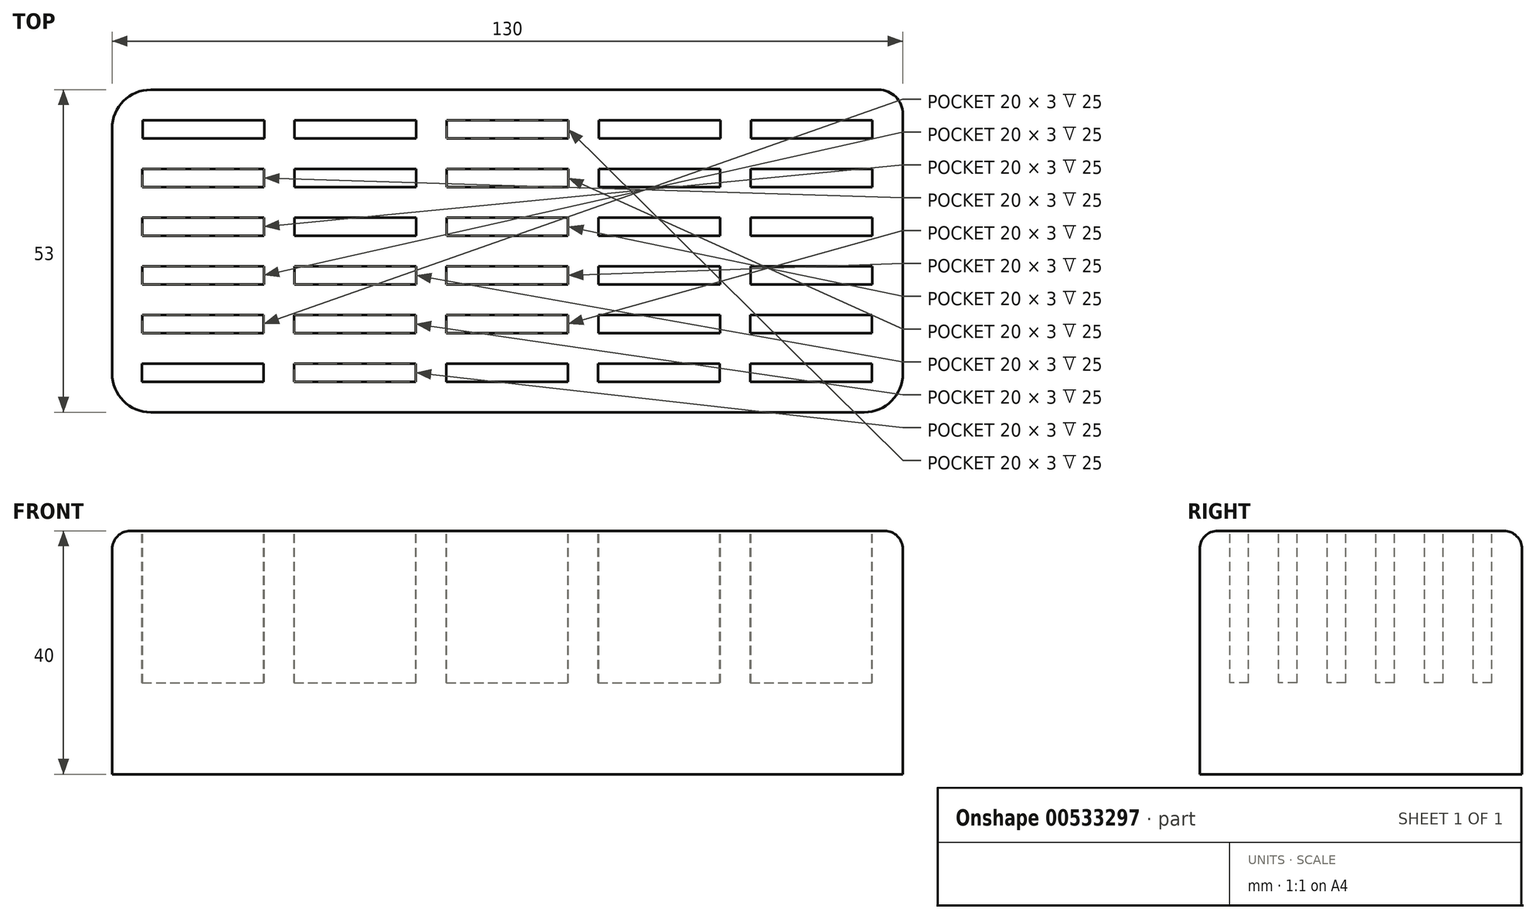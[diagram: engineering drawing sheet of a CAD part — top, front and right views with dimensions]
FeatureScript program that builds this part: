
annotation { "Feature Type Name" : "Feature", "Feature Type Description" : "" }
export const myFeature = defineFeature(function(context is Context, id is Id, definition is map)
    precondition{}
    {
        {
            var Q0;
            Q0=qCreatedBy(makeId("Top.planeOp"),FACE);
            var sketch = newSketch(context, id + "F0", { "sketchPlane" : qUnion([Q0])});
            skLineSegment(sketch, "E0.bottom", {"start": v(-58.22, 28.45) * mm, "end": v(61.43, 28.45) * mm});
            skLineSegment(sketch, "E0.top", {"start": v(-58.22, -24.55) * mm, "end": v(59.08, -24.55) * mm});
            skLineSegment(sketch, "E0.left", {"start": v(-64.57, 22.1) * mm, "end": v(-64.57, -18.2) * mm});
            skLineSegment(sketch, "E0.right", {"start": v(65.43, 24.45) * mm, "end": v(65.43, -18.2) * mm});
            skPoint(sketch, "E1.visualSharp", {"position": v(-64.57, 28.45) * mm});
            skArc(sketch, "E1.filletArc", {"start": v(-58.22, 28.45) * mm, "mid": v(-62.71, 26.59) * mm, "end": v(-64.57, 22.1) * mm});
            skPoint(sketch, "E2.visualSharp", {"position": v(65.43, 28.45) * mm});
            skArc(sketch, "E2.filletArc", {"start": v(65.43, 24.45) * mm, "mid": v(64.26, 27.27) * mm, "end": v(61.43, 28.45) * mm});
            skPoint(sketch, "E3.visualSharp", {"position": v(65.43, -24.55) * mm});
            skArc(sketch, "E3.filletArc", {"start": v(59.08, -24.55) * mm, "mid": v(63.57, -22.7) * mm, "end": v(65.43, -18.2) * mm});
            skPoint(sketch, "E4.visualSharp", {"position": v(-64.57, -24.55) * mm});
            skArc(sketch, "E4.filletArc", {"start": v(-64.57, -18.2) * mm, "mid": v(-62.71, -22.7) * mm, "end": v(-58.22, -24.55) * mm});
            skSolve(sketch);
        }
        {
            var Q0;
            Q0 = qSketchRegion(id + "F0", true);
            extrude(context, id + "F1", {"entities" : qUnion([Q0]), "depth" : 40 * mm, "offsetDistance" : 25.4 * mm});
        }
        {
            var Q0;
            Q0=makeQuery(id+"F1.opExtrude","CAP_FACE",FACE,{"disambiguationData":[OSD([sQuery(id+"F0.wireOp",EDGE,"E0.bottom"),sQuery(id+"F0.wireOp",EDGE,"E0.top"),sQuery(id+"F0.wireOp",EDGE,"E0.left"),sQuery(id+"F0.wireOp",EDGE,"E0.right"),sQuery(id+"F0.wireOp",EDGE,"E1.filletArc"),sQuery(id+"F0.wireOp",EDGE,"E2.filletArc"),sQuery(id+"F0.wireOp",EDGE,"E3.filletArc"),sQuery(id+"F0.wireOp",EDGE,"E4.filletArc")])],"isStart":false});
            var sketch = newSketch(context, id + "F2", { "sketchPlane" : qUnion([Q0])});
            skLineSegment(sketch, "E5.bottom", {"start": v(-59.57, 23.45) * mm, "end": v(-39.57, 23.45) * mm});
            skLineSegment(sketch, "E5.top", {"start": v(-59.57, 20.45) * mm, "end": v(-39.57, 20.45) * mm});
            skLineSegment(sketch, "E5.left", {"start": v(-59.57, 23.45) * mm, "end": v(-59.57, 20.45) * mm});
            skLineSegment(sketch, "E5.right", {"start": v(-39.57, 23.45) * mm, "end": v(-39.57, 20.45) * mm});
            skLineSegment(sketch, "E6.0.1.0", {"start": v(-59.59, 15.45) * mm, "end": v(-59.59, 12.45) * mm});
            skLineSegment(sketch, "E6.0.1.1", {"start": v(-59.59, 15.45) * mm, "end": v(-39.59, 15.45) * mm});
            skLineSegment(sketch, "E6.0.1.2", {"start": v(-39.59, 15.45) * mm, "end": v(-39.59, 12.45) * mm});
            skLineSegment(sketch, "E6.0.1.3", {"start": v(-59.59, 12.45) * mm, "end": v(-39.59, 12.45) * mm});
            skLineSegment(sketch, "E6.0.2.0", {"start": v(-59.6, 7.45) * mm, "end": v(-59.6, 4.45) * mm});
            skLineSegment(sketch, "E6.0.2.1", {"start": v(-59.6, 7.45) * mm, "end": v(-39.6, 7.45) * mm});
            skLineSegment(sketch, "E6.0.2.2", {"start": v(-39.6, 7.45) * mm, "end": v(-39.6, 4.45) * mm});
            skLineSegment(sketch, "E6.0.2.3", {"start": v(-59.6, 4.45) * mm, "end": v(-39.6, 4.45) * mm});
            skLineSegment(sketch, "E6.0.3.0", {"start": v(-59.62, -0.55) * mm, "end": v(-59.62, -3.55) * mm});
            skLineSegment(sketch, "E6.0.3.1", {"start": v(-59.62, -0.55) * mm, "end": v(-39.62, -0.55) * mm});
            skLineSegment(sketch, "E6.0.3.2", {"start": v(-39.62, -0.55) * mm, "end": v(-39.62, -3.55) * mm});
            skLineSegment(sketch, "E6.0.3.3", {"start": v(-59.62, -3.55) * mm, "end": v(-39.62, -3.55) * mm});
            skLineSegment(sketch, "E6.0.4.0", {"start": v(-59.64, -8.55) * mm, "end": v(-59.64, -11.55) * mm});
            skLineSegment(sketch, "E6.0.4.1", {"start": v(-59.64, -8.55) * mm, "end": v(-39.64, -8.55) * mm});
            skLineSegment(sketch, "E6.0.4.2", {"start": v(-39.64, -8.55) * mm, "end": v(-39.64, -11.55) * mm});
            skLineSegment(sketch, "E6.0.4.3", {"start": v(-59.64, -11.55) * mm, "end": v(-39.64, -11.55) * mm});
            skLineSegment(sketch, "E6.0.5.0", {"start": v(-59.66, -16.55) * mm, "end": v(-59.66, -19.55) * mm});
            skLineSegment(sketch, "E6.0.5.1", {"start": v(-59.66, -16.55) * mm, "end": v(-39.66, -16.55) * mm});
            skLineSegment(sketch, "E6.0.5.2", {"start": v(-39.66, -16.55) * mm, "end": v(-39.66, -19.55) * mm});
            skLineSegment(sketch, "E6.0.5.3", {"start": v(-59.66, -19.55) * mm, "end": v(-39.66, -19.55) * mm});
            skLineSegment(sketch, "E6.1.0.0", {"start": v(-34.57, 23.45) * mm, "end": v(-34.57, 20.45) * mm});
            skLineSegment(sketch, "E6.1.0.1", {"start": v(-34.57, 23.45) * mm, "end": v(-14.57, 23.45) * mm});
            skLineSegment(sketch, "E6.1.0.2", {"start": v(-14.57, 23.45) * mm, "end": v(-14.57, 20.45) * mm});
            skLineSegment(sketch, "E6.1.0.3", {"start": v(-34.57, 20.45) * mm, "end": v(-14.57, 20.45) * mm});
            skLineSegment(sketch, "E6.1.1.0", {"start": v(-34.59, 15.45) * mm, "end": v(-34.59, 12.45) * mm});
            skLineSegment(sketch, "E6.1.1.1", {"start": v(-34.59, 15.45) * mm, "end": v(-14.59, 15.45) * mm});
            skLineSegment(sketch, "E6.1.1.2", {"start": v(-14.59, 15.45) * mm, "end": v(-14.59, 12.45) * mm});
            skLineSegment(sketch, "E6.1.1.3", {"start": v(-34.59, 12.45) * mm, "end": v(-14.59, 12.45) * mm});
            skLineSegment(sketch, "E6.1.2.0", {"start": v(-34.6, 7.45) * mm, "end": v(-34.6, 4.45) * mm});
            skLineSegment(sketch, "E6.1.2.1", {"start": v(-34.6, 7.45) * mm, "end": v(-14.6, 7.45) * mm});
            skLineSegment(sketch, "E6.1.2.2", {"start": v(-14.6, 7.45) * mm, "end": v(-14.6, 4.45) * mm});
            skLineSegment(sketch, "E6.1.2.3", {"start": v(-34.6, 4.45) * mm, "end": v(-14.6, 4.45) * mm});
            skLineSegment(sketch, "E6.1.3.0", {"start": v(-34.62, -0.55) * mm, "end": v(-34.62, -3.55) * mm});
            skLineSegment(sketch, "E6.1.3.1", {"start": v(-34.62, -0.55) * mm, "end": v(-14.62, -0.55) * mm});
            skLineSegment(sketch, "E6.1.3.2", {"start": v(-14.62, -0.55) * mm, "end": v(-14.62, -3.55) * mm});
            skLineSegment(sketch, "E6.1.3.3", {"start": v(-34.62, -3.55) * mm, "end": v(-14.62, -3.55) * mm});
            skLineSegment(sketch, "E6.1.4.0", {"start": v(-34.64, -8.55) * mm, "end": v(-34.64, -11.55) * mm});
            skLineSegment(sketch, "E6.1.4.1", {"start": v(-34.64, -8.55) * mm, "end": v(-14.64, -8.55) * mm});
            skLineSegment(sketch, "E6.1.4.2", {"start": v(-14.64, -8.55) * mm, "end": v(-14.64, -11.55) * mm});
            skLineSegment(sketch, "E6.1.4.3", {"start": v(-34.64, -11.55) * mm, "end": v(-14.64, -11.55) * mm});
            skLineSegment(sketch, "E6.1.5.0", {"start": v(-34.66, -16.55) * mm, "end": v(-34.66, -19.55) * mm});
            skLineSegment(sketch, "E6.1.5.1", {"start": v(-34.66, -16.55) * mm, "end": v(-14.66, -16.55) * mm});
            skLineSegment(sketch, "E6.1.5.2", {"start": v(-14.66, -16.55) * mm, "end": v(-14.66, -19.55) * mm});
            skLineSegment(sketch, "E6.1.5.3", {"start": v(-34.66, -19.55) * mm, "end": v(-14.66, -19.55) * mm});
            skLineSegment(sketch, "E6.2.0.0", {"start": v(-9.57, 23.45) * mm, "end": v(-9.57, 20.45) * mm});
            skLineSegment(sketch, "E6.2.0.1", {"start": v(-9.57, 23.45) * mm, "end": v(10.43, 23.45) * mm});
            skLineSegment(sketch, "E6.2.0.2", {"start": v(10.43, 23.45) * mm, "end": v(10.43, 20.45) * mm});
            skLineSegment(sketch, "E6.2.0.3", {"start": v(-9.57, 20.45) * mm, "end": v(10.43, 20.45) * mm});
            skLineSegment(sketch, "E6.2.1.0", {"start": v(-9.59, 15.45) * mm, "end": v(-9.59, 12.45) * mm});
            skLineSegment(sketch, "E6.2.1.1", {"start": v(-9.59, 15.45) * mm, "end": v(10.41, 15.45) * mm});
            skLineSegment(sketch, "E6.2.1.2", {"start": v(10.41, 15.45) * mm, "end": v(10.41, 12.45) * mm});
            skLineSegment(sketch, "E6.2.1.3", {"start": v(-9.59, 12.45) * mm, "end": v(10.41, 12.45) * mm});
            skLineSegment(sketch, "E6.2.2.0", {"start": v(-9.6, 7.45) * mm, "end": v(-9.6, 4.45) * mm});
            skLineSegment(sketch, "E6.2.2.1", {"start": v(-9.6, 7.45) * mm, "end": v(10.4, 7.45) * mm});
            skLineSegment(sketch, "E6.2.2.2", {"start": v(10.4, 7.45) * mm, "end": v(10.4, 4.45) * mm});
            skLineSegment(sketch, "E6.2.2.3", {"start": v(-9.6, 4.45) * mm, "end": v(10.4, 4.45) * mm});
            skLineSegment(sketch, "E6.2.3.0", {"start": v(-9.62, -0.55) * mm, "end": v(-9.62, -3.55) * mm});
            skLineSegment(sketch, "E6.2.3.1", {"start": v(-9.62, -0.55) * mm, "end": v(10.38, -0.55) * mm});
            skLineSegment(sketch, "E6.2.3.2", {"start": v(10.38, -0.55) * mm, "end": v(10.38, -3.55) * mm});
            skLineSegment(sketch, "E6.2.3.3", {"start": v(-9.62, -3.55) * mm, "end": v(10.38, -3.55) * mm});
            skLineSegment(sketch, "E6.2.4.0", {"start": v(-9.64, -8.55) * mm, "end": v(-9.64, -11.55) * mm});
            skLineSegment(sketch, "E6.2.4.1", {"start": v(-9.64, -8.55) * mm, "end": v(10.36, -8.55) * mm});
            skLineSegment(sketch, "E6.2.4.2", {"start": v(10.36, -8.55) * mm, "end": v(10.36, -11.55) * mm});
            skLineSegment(sketch, "E6.2.4.3", {"start": v(-9.64, -11.55) * mm, "end": v(10.36, -11.55) * mm});
            skLineSegment(sketch, "E6.2.5.0", {"start": v(-9.66, -16.55) * mm, "end": v(-9.66, -19.55) * mm});
            skLineSegment(sketch, "E6.2.5.1", {"start": v(-9.66, -16.55) * mm, "end": v(10.34, -16.55) * mm});
            skLineSegment(sketch, "E6.2.5.2", {"start": v(10.34, -16.55) * mm, "end": v(10.34, -19.55) * mm});
            skLineSegment(sketch, "E6.2.5.3", {"start": v(-9.66, -19.55) * mm, "end": v(10.34, -19.55) * mm});
            skLineSegment(sketch, "E6.3.0.0", {"start": v(15.43, 23.45) * mm, "end": v(15.43, 20.45) * mm});
            skLineSegment(sketch, "E6.3.0.1", {"start": v(15.43, 23.45) * mm, "end": v(35.43, 23.45) * mm});
            skLineSegment(sketch, "E6.3.0.2", {"start": v(35.43, 23.45) * mm, "end": v(35.43, 20.45) * mm});
            skLineSegment(sketch, "E6.3.0.3", {"start": v(15.43, 20.45) * mm, "end": v(35.43, 20.45) * mm});
            skLineSegment(sketch, "E6.3.1.0", {"start": v(15.41, 15.45) * mm, "end": v(15.41, 12.45) * mm});
            skLineSegment(sketch, "E6.3.1.1", {"start": v(15.41, 15.45) * mm, "end": v(35.41, 15.45) * mm});
            skLineSegment(sketch, "E6.3.1.2", {"start": v(35.41, 15.45) * mm, "end": v(35.41, 12.45) * mm});
            skLineSegment(sketch, "E6.3.1.3", {"start": v(15.41, 12.45) * mm, "end": v(35.41, 12.45) * mm});
            skLineSegment(sketch, "E6.3.2.0", {"start": v(15.4, 7.45) * mm, "end": v(15.4, 4.45) * mm});
            skLineSegment(sketch, "E6.3.2.1", {"start": v(15.4, 7.45) * mm, "end": v(35.4, 7.45) * mm});
            skLineSegment(sketch, "E6.3.2.2", {"start": v(35.4, 7.45) * mm, "end": v(35.4, 4.45) * mm});
            skLineSegment(sketch, "E6.3.2.3", {"start": v(15.4, 4.45) * mm, "end": v(35.4, 4.45) * mm});
            skLineSegment(sketch, "E6.3.3.0", {"start": v(15.38, -0.55) * mm, "end": v(15.38, -3.55) * mm});
            skLineSegment(sketch, "E6.3.3.1", {"start": v(15.38, -0.55) * mm, "end": v(35.38, -0.55) * mm});
            skLineSegment(sketch, "E6.3.3.2", {"start": v(35.38, -0.55) * mm, "end": v(35.38, -3.55) * mm});
            skLineSegment(sketch, "E6.3.3.3", {"start": v(15.38, -3.55) * mm, "end": v(35.38, -3.55) * mm});
            skLineSegment(sketch, "E6.3.4.0", {"start": v(15.36, -8.55) * mm, "end": v(15.36, -11.55) * mm});
            skLineSegment(sketch, "E6.3.4.1", {"start": v(15.36, -8.55) * mm, "end": v(35.36, -8.55) * mm});
            skLineSegment(sketch, "E6.3.4.2", {"start": v(35.36, -8.55) * mm, "end": v(35.36, -11.55) * mm});
            skLineSegment(sketch, "E6.3.4.3", {"start": v(15.36, -11.55) * mm, "end": v(35.36, -11.55) * mm});
            skLineSegment(sketch, "E6.3.5.0", {"start": v(15.34, -16.55) * mm, "end": v(15.34, -19.55) * mm});
            skLineSegment(sketch, "E6.3.5.1", {"start": v(15.34, -16.55) * mm, "end": v(35.34, -16.55) * mm});
            skLineSegment(sketch, "E6.3.5.2", {"start": v(35.34, -16.55) * mm, "end": v(35.34, -19.55) * mm});
            skLineSegment(sketch, "E6.3.5.3", {"start": v(15.34, -19.55) * mm, "end": v(35.34, -19.55) * mm});
            skLineSegment(sketch, "E6.4.0.0", {"start": v(40.43, 23.45) * mm, "end": v(40.43, 20.45) * mm});
            skLineSegment(sketch, "E6.4.0.1", {"start": v(40.43, 23.45) * mm, "end": v(60.43, 23.45) * mm});
            skLineSegment(sketch, "E6.4.0.2", {"start": v(60.43, 23.45) * mm, "end": v(60.43, 20.45) * mm});
            skLineSegment(sketch, "E6.4.0.3", {"start": v(40.43, 20.45) * mm, "end": v(60.43, 20.45) * mm});
            skLineSegment(sketch, "E6.4.1.0", {"start": v(40.41, 15.45) * mm, "end": v(40.41, 12.45) * mm});
            skLineSegment(sketch, "E6.4.1.1", {"start": v(40.41, 15.45) * mm, "end": v(60.41, 15.45) * mm});
            skLineSegment(sketch, "E6.4.1.2", {"start": v(60.41, 15.45) * mm, "end": v(60.41, 12.45) * mm});
            skLineSegment(sketch, "E6.4.1.3", {"start": v(40.41, 12.45) * mm, "end": v(60.41, 12.45) * mm});
            skLineSegment(sketch, "E6.4.2.0", {"start": v(40.4, 7.45) * mm, "end": v(40.4, 4.45) * mm});
            skLineSegment(sketch, "E6.4.2.1", {"start": v(40.4, 7.45) * mm, "end": v(60.4, 7.45) * mm});
            skLineSegment(sketch, "E6.4.2.2", {"start": v(60.4, 7.45) * mm, "end": v(60.4, 4.45) * mm});
            skLineSegment(sketch, "E6.4.2.3", {"start": v(40.4, 4.45) * mm, "end": v(60.4, 4.45) * mm});
            skLineSegment(sketch, "E6.4.3.0", {"start": v(40.38, -0.55) * mm, "end": v(40.38, -3.55) * mm});
            skLineSegment(sketch, "E6.4.3.1", {"start": v(40.38, -0.55) * mm, "end": v(60.38, -0.55) * mm});
            skLineSegment(sketch, "E6.4.3.2", {"start": v(60.38, -0.55) * mm, "end": v(60.38, -3.55) * mm});
            skLineSegment(sketch, "E6.4.3.3", {"start": v(40.38, -3.55) * mm, "end": v(60.38, -3.55) * mm});
            skLineSegment(sketch, "E6.4.4.0", {"start": v(40.36, -8.55) * mm, "end": v(40.36, -11.55) * mm});
            skLineSegment(sketch, "E6.4.4.1", {"start": v(40.36, -8.55) * mm, "end": v(60.36, -8.55) * mm});
            skLineSegment(sketch, "E6.4.4.2", {"start": v(60.36, -8.55) * mm, "end": v(60.36, -11.55) * mm});
            skLineSegment(sketch, "E6.4.4.3", {"start": v(40.36, -11.55) * mm, "end": v(60.36, -11.55) * mm});
            skLineSegment(sketch, "E6.4.5.0", {"start": v(40.34, -16.55) * mm, "end": v(40.34, -19.55) * mm});
            skLineSegment(sketch, "E6.4.5.1", {"start": v(40.34, -16.55) * mm, "end": v(60.34, -16.55) * mm});
            skLineSegment(sketch, "E6.4.5.2", {"start": v(60.34, -16.55) * mm, "end": v(60.34, -19.55) * mm});
            skLineSegment(sketch, "E6.4.5.3", {"start": v(40.34, -19.55) * mm, "end": v(60.34, -19.55) * mm});
            skLineSegment(sketch, "E6.direction1", {"start": v(-59.57, 20.45) * mm, "end": v(-34.57, 20.45) * mm, "construction": true});
            skLineSegment(sketch, "E6.direction2", {"start": v(-59.57, 20.45) * mm, "end": v(-59.59, 12.45) * mm, "construction": true});
            skSolve(sketch);
        }
        {
            var Q0;
            Q0 = qSketchRegion(id + "F2", true);
            extrude(context, id + "F3", {"entities" : qUnion([Q0]), "operationType" : NewBodyOperationType.REMOVE, "oppositeDirection" : true, "depth" : 25 * mm, "offsetDistance" : 25.4 * mm});
        }
        {
            var Q0;
            Q0=makeQuery(id+"F1.opExtrude","CAP_EDGE",EDGE,{"disambiguationData":[OSD([sQuery(id+"F0.wireOp",EDGE,"E0.bottom")])],"isStart":false});
            fillet(context, id + "F4", {"entities" : qUnion([Q0]), "radius" : 3 * mm, "tangentPropagation" : true, "allowEdgeOverflow" : false});
        }
    });
